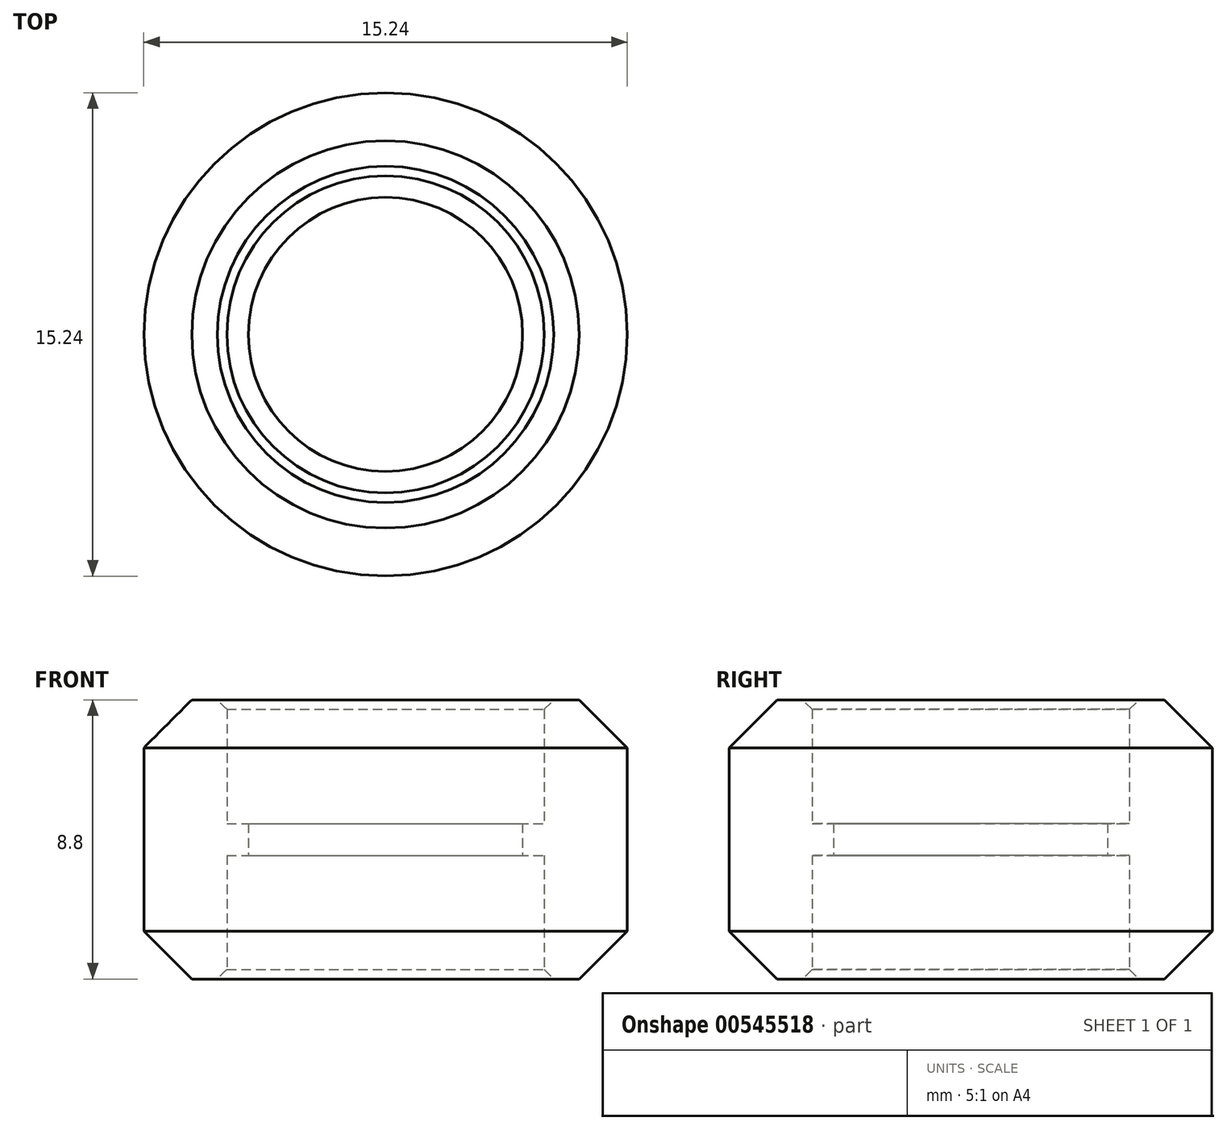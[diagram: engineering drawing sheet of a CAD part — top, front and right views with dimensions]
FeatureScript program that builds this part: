
annotation { "Feature Type Name" : "Feature", "Feature Type Description" : "" }
export const myFeature = defineFeature(function(context is Context, id is Id, definition is map)
    precondition{}
    {
        {
            var Q0;
            Q0=qCreatedBy(makeId("Front.planeOp"),FACE);
            var sketch = newSketch(context, id + "F0", { "sketchPlane" : qUnion([Q0])});
            skLineSegment(sketch, "E0", {"start": v(-5.3, 4.4) * mm, "end": v(-6.1, 4.4) * mm});
            skLineSegment(sketch, "E1", {"start": v(-6.1, 4.4) * mm, "end": v(-7.62, 2.89) * mm});
            skLineSegment(sketch, "E2", {"start": v(-7.62, 2.89) * mm, "end": v(-7.61, -2.9) * mm});
            skLineSegment(sketch, "E3", {"start": v(-7.61, -2.9) * mm, "end": v(-6.1, -4.4) * mm});
            skLineSegment(sketch, "E4", {"start": v(-6.1, -4.4) * mm, "end": v(-5.3, -4.4) * mm});
            skLineSegment(sketch, "E5", {"start": v(-5, 4.1) * mm, "end": v(-5, 0.5) * mm});
            skLineSegment(sketch, "E6", {"start": v(-5, 0.5) * mm, "end": v(-4.32, 0.5) * mm});
            skLineSegment(sketch, "E7", {"start": v(-4.32, 0.5) * mm, "end": v(-4.32, -0.5) * mm});
            skLineSegment(sketch, "E8", {"start": v(-4.32, -0.5) * mm, "end": v(-5, -0.5) * mm});
            skLineSegment(sketch, "E9", {"start": v(-5, -0.5) * mm, "end": v(-5, -4.1) * mm});
            skLineSegment(sketch, "E10", {"start": v(-5.3, 4.4) * mm, "end": v(-5, 4.1) * mm});
            skLineSegment(sketch, "E11.MirrorCS", {"start": v(-5.3, -4.4) * mm, "end": v(-5, -4.1) * mm});
            skLineSegment(sketch, "E12", {"start": v(0, 0) * mm, "end": v(-2.59, 0) * mm, "construction": true});
            skLineSegment(sketch, "E13", {"start": v(0, -4.4) * mm, "end": v(0, 4.4) * mm, "construction": true});
            skPoint(sketch, "E14", {"position": v(-4.32, 0) * mm});
            skSolve(sketch);
        }
        {
            var Q0;
            Q0=makeQuery(id+"F0.imprint","IMPRINT",FACE,{"disambiguationData":[TD([[makeQuery(id+"F0.imprint","IMPRINT",EDGE,{"derivedFrom":sQuery(id+"F0.wireOp",EDGE,"E0")}),1.0]])]});
            var Q1;
            Q1=sQuery(id+"F0.wireOp",EDGE,"E13");
            revolve(context, id + "F1", {"surfaceOperationType" : NewSurfaceOperationType.NEW, "entities" : qUnion([Q0]), "axis" : qUnion([Q1]), "revolveType" : RevolveType.FULL});
        }
        {
            var Q0;
            Q0 = qSketchRegion(id + "F0", true);
            var Q1;
            Q1=sQuery(id+"F0.wireOp",EDGE,"E13");
            revolve(context, id + "F2", {"surfaceOperationType" : NewSurfaceOperationType.NEW, "entities" : qUnion([Q0]), "axis" : qUnion([Q1]), "revolveType" : RevolveType.FULL});
        }
    });
